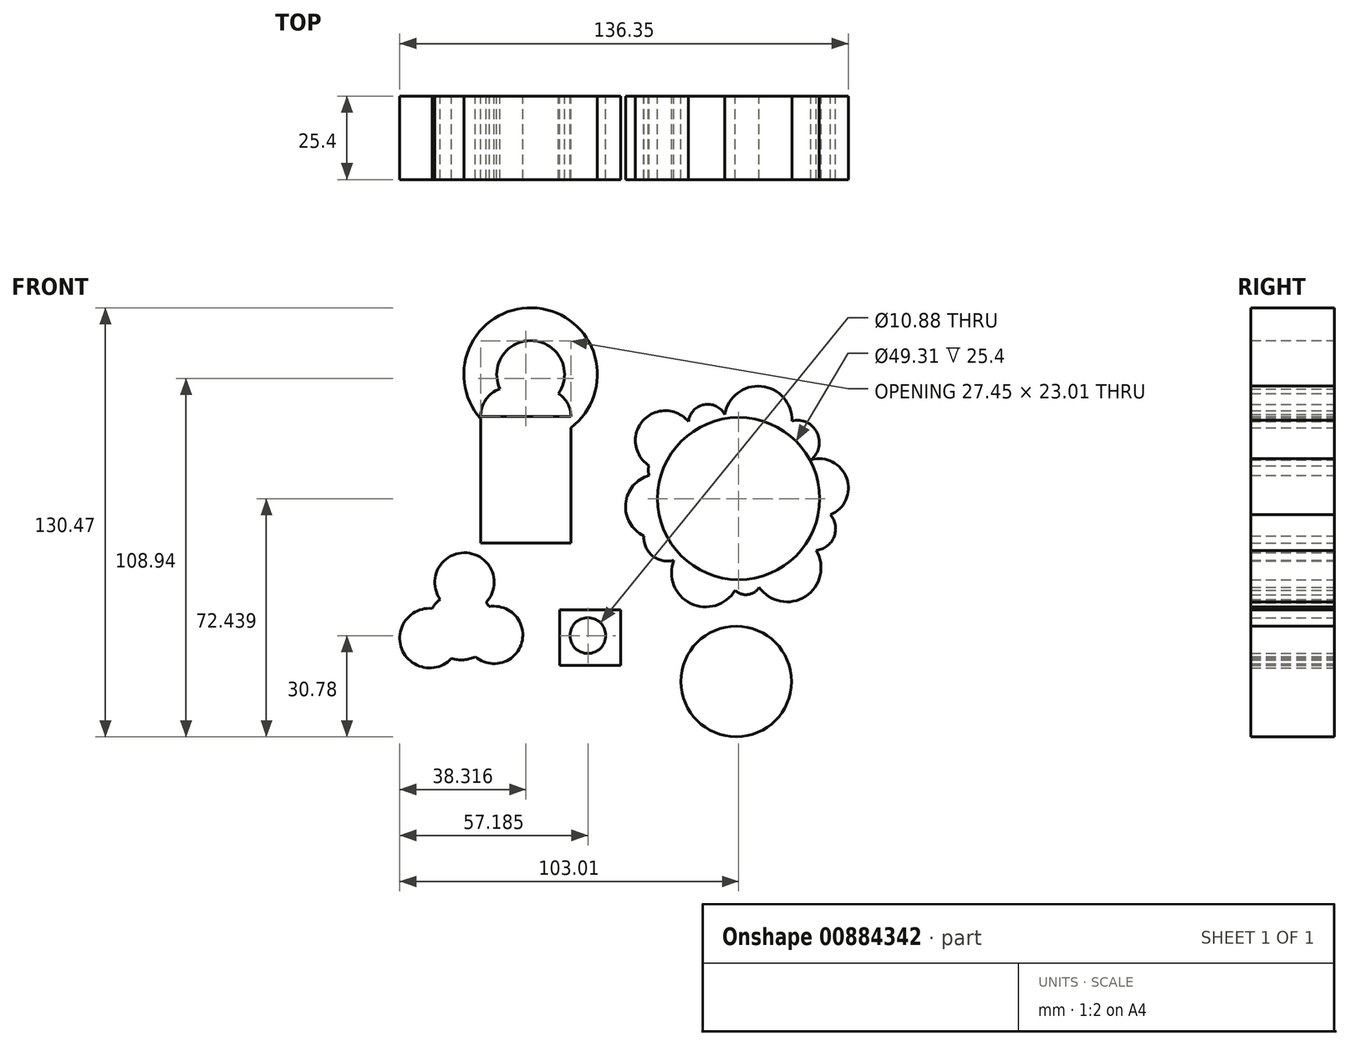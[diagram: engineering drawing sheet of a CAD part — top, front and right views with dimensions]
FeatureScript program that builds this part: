
annotation { "Feature Type Name" : "Feature", "Feature Type Description" : "" }
export const myFeature = defineFeature(function(context is Context, id is Id, definition is map)
    precondition{}
    {
        {
            var Q0;
            Q0=qCreatedBy(makeId("Front.planeOp"),FACE);
            var sketch = newSketch(context, id + "F0", { "sketchPlane" : qUnion([Q0])});
            skCircle(sketch, "E0", {"center": v(-48.4, -21.8) * mm, "radius": 10.34 * mm});
            skCircle(sketch, "E1", {"center": v(-47.42, -8.58) * mm, "radius": 9.01 * mm});
            skCircle(sketch, "E2", {"center": v(-38.43, -24.57) * mm, "radius": 8.74 * mm});
            skCircle(sketch, "E3", {"center": v(-58.05, -25.53) * mm, "radius": 9.07 * mm});
            skLineSegment(sketch, "E4.bottom", {"start": v(-42.52, 41.9) * mm, "end": v(-15.07, 41.9) * mm});
            skLineSegment(sketch, "E4.top", {"start": v(-42.52, 3.43) * mm, "end": v(-15.07, 3.43) * mm});
            skLineSegment(sketch, "E4.left", {"start": v(-42.52, 41.9) * mm, "end": v(-42.52, 3.43) * mm});
            skLineSegment(sketch, "E4.right", {"start": v(-15.07, 41.9) * mm, "end": v(-15.07, 3.43) * mm});
            skArc(sketch, "E5", {"start": v(-15.07, 41.9) * mm, "mid": v(-19.4, 49.14) * mm, "end": v(-27.81, 48.77) * mm});
            skArc(sketch, "E6", {"start": v(-27.81, 48.77) * mm, "mid": v(-37.35, 50.02) * mm, "end": v(-42.52, 41.9) * mm});
            skCircle(sketch, "E7", {"center": v(-27.32, 54.65) * mm, "radius": 20.3 * mm});
            skCircle(sketch, "E8", {"center": v(35.9, 16.9) * mm, "radius": 24.65 * mm});
            skCircle(sketch, "E9", {"center": v(13.6, 34.55) * mm, "radius": 9.08 * mm});
            skCircle(sketch, "E10", {"center": v(41.82, 40.84) * mm, "radius": 10.27 * mm});
            skCircle(sketch, "E11", {"center": v(60.34, 20.15) * mm, "radius": 8.9 * mm});
            skCircle(sketch, "E12", {"center": v(50.6, -4.17) * mm, "radius": 10.34 * mm});
            skCircle(sketch, "E13", {"center": v(25.9, -5.62) * mm, "radius": 10.41 * mm});
            skCircle(sketch, "E14", {"center": v(11.37, 14.48) * mm, "radius": 9.85 * mm});
            skCircle(sketch, "E15", {"center": v(26.5, 39.7) * mm, "radius": 5.9 * mm});
            skCircle(sketch, "E16", {"center": v(53.7, 33.97) * mm, "radius": 6.74 * mm});
            skCircle(sketch, "E17", {"center": v(58.78, 7.72) * mm, "radius": 6.59 * mm});
            skCircle(sketch, "E18", {"center": v(38.11, -7.65) * mm, "radius": 4.69 * mm});
            skCircle(sketch, "E19", {"center": v(14.28, 5.07) * mm, "radius": 7.2 * mm});
            skCircle(sketch, "E20", {"center": v(12.8, 25.5) * mm, "radius": 4.36 * mm});
            skCircle(sketch, "E21", {"center": v(35.9, 16.9) * mm, "radius": 10.34 * mm});
            skLineSegment(sketch, "E22.bottom", {"start": v(0, -33.82) * mm, "end": v(-18.5, -33.82) * mm});
            skLineSegment(sketch, "E22.top", {"start": v(0, -16.9) * mm, "end": v(-18.5, -16.9) * mm});
            skLineSegment(sketch, "E22.left", {"start": v(0, -33.82) * mm, "end": v(0, -16.9) * mm});
            skLineSegment(sketch, "E22.right", {"start": v(-18.5, -33.82) * mm, "end": v(-18.5, -16.9) * mm});
            skLineSegment(sketch, "E23", {"start": v(-18.5, -16.9) * mm, "end": v(-24.87, -8.58) * mm});
            skLineSegment(sketch, "E24", {"start": v(0, -16.9) * mm, "end": v(5.76, -11.52) * mm});
            skLineSegment(sketch, "E25", {"start": v(0, -33.82) * mm, "end": v(5.76, -38.47) * mm});
            skLineSegment(sketch, "E26", {"start": v(-18.5, -33.82) * mm, "end": v(-23.9, -38.88) * mm});
            skCircle(sketch, "E27", {"center": v(-9.92, -24.75) * mm, "radius": 5.44 * mm});
            skCircle(sketch, "E28", {"center": v(-9.92, -24.75) * mm, "radius": 3.44 * mm});
            skCircle(sketch, "E29", {"center": v(-9.92, -24.75) * mm, "radius": 1.5 * mm});
            skCircle(sketch, "E30", {"center": v(-27.32, 54.65) * mm, "radius": 10.3 * mm});
            skCircle(sketch, "E31", {"center": v(-27.32, 54.65) * mm, "radius": 4.62 * mm});
            skCircle(sketch, "E32", {"center": v(35.9, 16.9) * mm, "radius": 5.28 * mm});
            skCircle(sketch, "E33", {"center": v(35.9, 16.9) * mm, "radius": 2.45 * mm});
            skCircle(sketch, "E34", {"center": v(35.9, 16.9) * mm, "radius": 13.73 * mm});
            skCircle(sketch, "E35", {"center": v(35.9, 16.9) * mm, "radius": 7.9 * mm});
            skCircle(sketch, "E36", {"center": v(35.17, -38.72) * mm, "radius": 16.81 * mm});
            skSolve(sketch);
        }
        {
            var Q0;
            Q0 = qSketchRegion(id + "F0", true);
            extrude(context, id + "F1", {"entities" : qUnion([Q0]), "depth" : 25.4 * mm, "offsetDistance" : 25.4 * mm});
        }
    });
